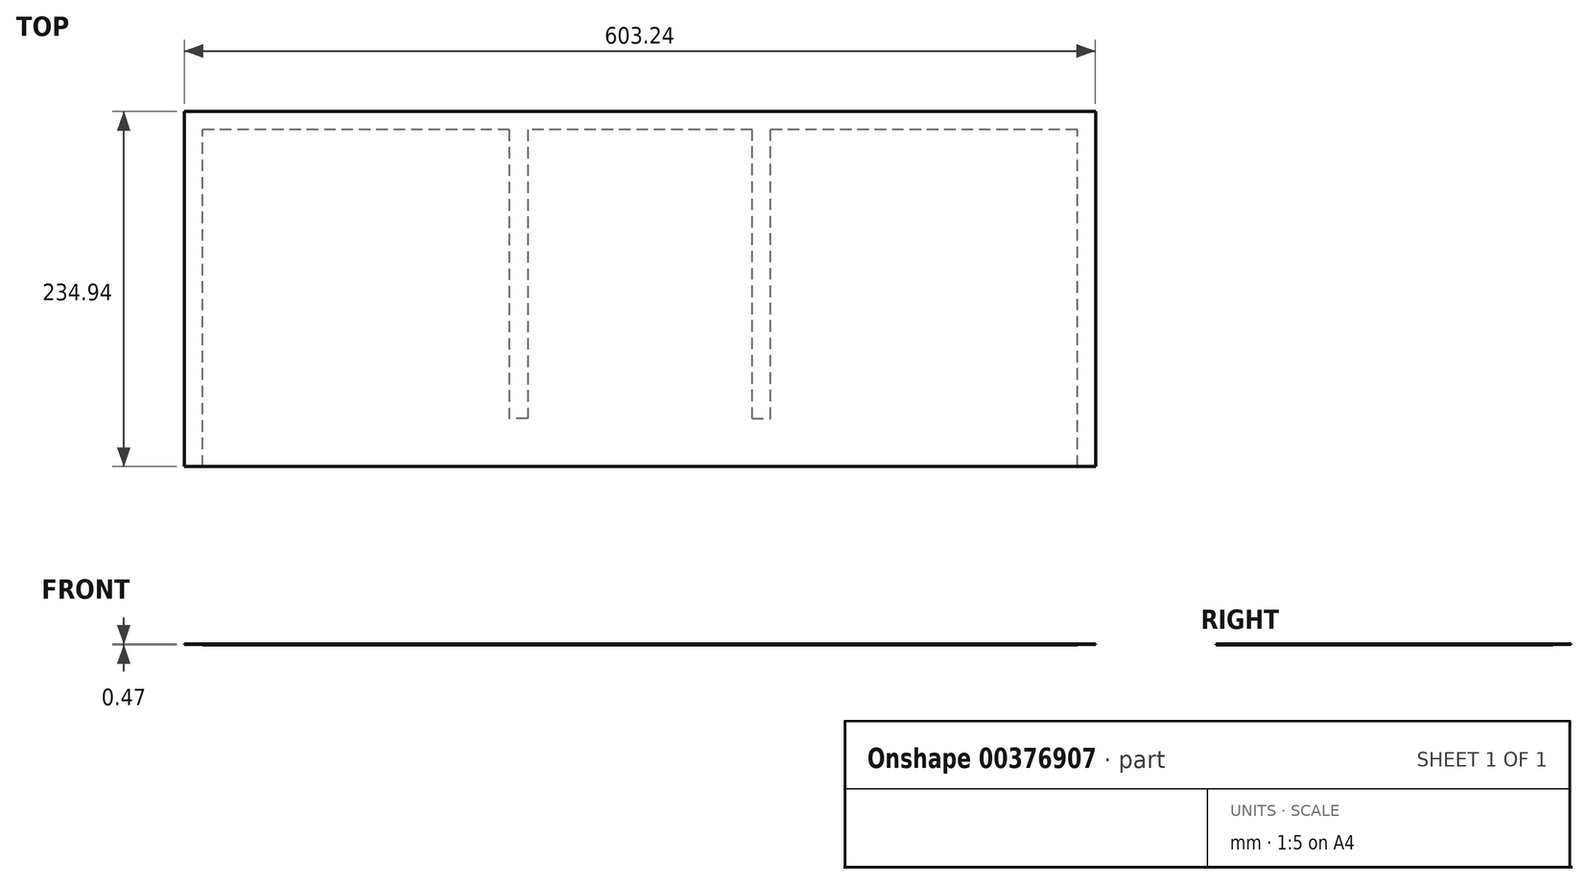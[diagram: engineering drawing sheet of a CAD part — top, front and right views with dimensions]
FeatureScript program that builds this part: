
annotation { "Feature Type Name" : "Feature", "Feature Type Description" : "" }
export const myFeature = defineFeature(function(context is Context, id is Id, definition is map)
    precondition{}
    {
        {
            assignVariable(context, id + "F0", {"name" : "material", "anyValue" : 0.47});
        }
        {
            var Q0;
            Q0=qCreatedBy(makeId("Top.planeOp"),FACE);
            var sketch = newSketch(context, id + "F1", { "sketchPlane" : qUnion([Q0])});
            skLineSegment(sketch, "E0.bottom", {"start": v(301.63, 117.48) * mm, "end": v(-301.63, 117.48) * mm});
            skLineSegment(sketch, "E0.top", {"start": v(301.63, -117.48) * mm, "end": v(-301.63, -117.48) * mm});
            skLineSegment(sketch, "E0.left", {"start": v(301.63, 117.48) * mm, "end": v(301.63, -117.48) * mm});
            skLineSegment(sketch, "E0.right", {"start": v(-301.63, 117.48) * mm, "end": v(-301.63, -117.48) * mm});
            skPoint(sketch, "E0.middle", {"position": v(0, 0) * mm});
            skSolve(sketch);
        }
        {
            var Q0;
            Q0=makeQuery(id+"F1.imprint","IMPRINT",FACE,{"disambiguationData":[TD([[makeQuery(id+"F1.imprint","IMPRINT",EDGE,{"derivedFrom":sQuery(id+"F1.wireOp",EDGE,"E0.bottom")}),1.0]])]});
            extrude(context, id + "F2", {"entities" : qUnion([Q0]), "depth" : (getVariable(context, 'material')) * mm});
        }
        {
            var Q0;
            Q0=makeQuery(id+"F2.opExtrude","CAP_FACE",FACE,{"disambiguationData":[OSD([sQuery(id+"F1.wireOp",EDGE,"E0.bottom"),sQuery(id+"F1.wireOp",EDGE,"E0.top"),sQuery(id+"F1.wireOp",EDGE,"E0.left"),sQuery(id+"F1.wireOp",EDGE,"E0.right")])],"isStart":true});
            var sketch = newSketch(context, id + "F3", { "sketchPlane" : qUnion([Q0])});
            skLineSegment(sketch, "E1.bottom", {"start": v(-301.63, 117.48) * mm, "end": v(-289.56, 117.48) * mm});
            skLineSegment(sketch, "E1.top", {"start": v(-301.63, -117.48) * mm, "end": v(-289.56, -117.48) * mm});
            skLineSegment(sketch, "E1.left", {"start": v(-301.63, 117.48) * mm, "end": v(-301.63, -117.48) * mm});
            skLineSegment(sketch, "E1.right", {"start": v(-289.56, 117.48) * mm, "end": v(-289.56, -117.48) * mm});
            skSolve(sketch);
        }
        {
            var Q0;
            Q0=makeQuery(id+"F3.imprint","IMPRINT",FACE,{"disambiguationData":[TD([[makeQuery(id+"F3.imprint","IMPRINT",EDGE,{"derivedFrom":sQuery(id+"F3.wireOp",EDGE,"E1.bottom")}),1.0]])]});
            extrude(context, id + "F4", {"entities" : qUnion([Q0]), "operationType" : NewBodyOperationType.REMOVE, "oppositeDirection" : true, "depth" : (getVariable(context, 'material') / 2) * mm});
        }
        {
            var Q0;
            Q0=makeQuery(id+"F2.opExtrude","CAP_FACE",FACE,{"disambiguationData":[OSD([sQuery(id+"F1.wireOp",EDGE,"E0.bottom"),sQuery(id+"F1.wireOp",EDGE,"E0.top"),sQuery(id+"F1.wireOp",EDGE,"E0.left"),sQuery(id+"F1.wireOp",EDGE,"E0.right")])],"isStart":true});
            var sketch = newSketch(context, id + "F5", { "sketchPlane" : qUnion([Q0])});
            skLineSegment(sketch, "E2.bottom", {"start": v(301.63, 117.48) * mm, "end": v(289.56, 117.48) * mm});
            skLineSegment(sketch, "E2.top", {"start": v(301.63, -117.48) * mm, "end": v(289.56, -117.48) * mm});
            skLineSegment(sketch, "E2.left", {"start": v(301.63, 117.48) * mm, "end": v(301.63, -117.48) * mm});
            skLineSegment(sketch, "E2.right", {"start": v(289.56, 117.48) * mm, "end": v(289.56, -117.48) * mm});
            skSolve(sketch);
        }
        {
            var Q0;
            Q0 = qSketchRegion(id + "F5", true);
            extrude(context, id + "F6", {"entities" : qUnion([Q0]), "operationType" : NewBodyOperationType.REMOVE, "oppositeDirection" : true, "depth" : (getVariable(context, 'material') / 2) * mm});
        }
        {
            var Q0;
            Q0=makeQuery(id+"F2.opExtrude","CAP_FACE",FACE,{"disambiguationData":[OSD([sQuery(id+"F1.wireOp",EDGE,"E0.bottom"),sQuery(id+"F1.wireOp",EDGE,"E0.top"),sQuery(id+"F1.wireOp",EDGE,"E0.left"),sQuery(id+"F1.wireOp",EDGE,"E0.right")])],"isStart":true});
            var sketch = newSketch(context, id + "F7", { "sketchPlane" : qUnion([Q0])});
            skLineSegment(sketch, "E3", {"start": v(289.56, 117.48) * mm, "end": v(86.36, 117.48) * mm, "construction": true});
            skLineSegment(sketch, "E4.bottom", {"start": v(86.36, 117.48) * mm, "end": v(74.3, 117.48) * mm});
            skLineSegment(sketch, "E4.top", {"start": v(86.36, -117.48) * mm, "end": v(74.3, -117.48) * mm});
            skLineSegment(sketch, "E4.left", {"start": v(86.36, 117.48) * mm, "end": v(86.36, -117.48) * mm});
            skLineSegment(sketch, "E4.right", {"start": v(74.3, 117.48) * mm, "end": v(74.3, -117.48) * mm});
            skSolve(sketch);
        }
        {
            var Q0;
            Q0 = qSketchRegion(id + "F7", true);
            extrude(context, id + "F8", {"entities" : qUnion([Q0]), "operationType" : NewBodyOperationType.REMOVE, "oppositeDirection" : true, "depth" : (getVariable(context, 'material') / 2) * mm});
        }
        {
            var Q0;
            {var subQ0=sQuery(id+"F1.wireOp",EDGE,"E0.bottom");var subQ1=sQuery(id+"F1.wireOp",EDGE,"E0.top");Q0=makeQuery(id+"F8.boolean.opBoolean","SPLIT",FACE,{"disambiguationData":[TD([makeQuery(id+"F4.boolean.opBoolean","COPY",FACE,{"derivedFrom":makeQuery(id+"F4.opExtrude","SWEPT_FACE",FACE,{"disambiguationData":[OSD([sQuery(id+"F3.wireOp",EDGE,"E1.right")])]})})])],"derivedFrom":makeQuery(id+"F2.opExtrude","CAP_FACE",FACE,{"disambiguationData":[OSD([subQ0,subQ1,sQuery(id+"F1.wireOp",EDGE,"E0.left"),sQuery(id+"F1.wireOp",EDGE,"E0.right")])],"isStart":true})});}
            var sketch = newSketch(context, id + "F9", { "sketchPlane" : qUnion([Q0])});
            skLineSegment(sketch, "E5", {"start": v(-289.56, -117.48) * mm, "end": v(-86.36, -117.48) * mm, "construction": true});
            skLineSegment(sketch, "E6.bottom", {"start": v(-86.36, -117.48) * mm, "end": v(-74.3, -117.48) * mm});
            skLineSegment(sketch, "E6.top", {"start": v(-86.36, 117.48) * mm, "end": v(-74.3, 117.48) * mm});
            skLineSegment(sketch, "E6.left", {"start": v(-86.36, -117.48) * mm, "end": v(-86.36, 117.48) * mm});
            skLineSegment(sketch, "E6.right", {"start": v(-74.3, -117.48) * mm, "end": v(-74.3, 117.48) * mm});
            skSolve(sketch);
        }
        {
            var Q0;
            Q0=makeQuery(id+"F9.imprint","IMPRINT",FACE,{"disambiguationData":[TD([[makeQuery(id+"F9.imprint","IMPRINT",EDGE,{"derivedFrom":sQuery(id+"F9.wireOp",EDGE,"E6.bottom")}),-1.0]])]});
            extrude(context, id + "F10", {"entities" : qUnion([Q0]), "operationType" : NewBodyOperationType.REMOVE, "oppositeDirection" : true, "depth" : (getVariable(context, 'material') / 2) * mm});
        }
        {
            var Q0;
            {var subQ0=sQuery(id+"F1.wireOp",EDGE,"E0.bottom");var subQ1=sQuery(id+"F1.wireOp",EDGE,"E0.top");Q0=makeQuery(id+"F8.boolean.opBoolean","SPLIT",FACE,{"disambiguationData":[TD([makeQuery(id+"F6.boolean.opBoolean","COPY",FACE,{"derivedFrom":makeQuery(id+"F6.opExtrude","SWEPT_FACE",FACE,{"disambiguationData":[OSD([sQuery(id+"F5.wireOp",EDGE,"E2.right")])]})})])],"derivedFrom":makeQuery(id+"F2.opExtrude","CAP_FACE",FACE,{"disambiguationData":[OSD([subQ0,subQ1,sQuery(id+"F1.wireOp",EDGE,"E0.left"),sQuery(id+"F1.wireOp",EDGE,"E0.right")])],"isStart":true})});}
            var sketch = newSketch(context, id + "F11", { "sketchPlane" : qUnion([Q0])});
            skLineSegment(sketch, "E7.bottom", {"start": v(289.56, -117.48) * mm, "end": v(86.36, -117.48) * mm});
            skLineSegment(sketch, "E7.top", {"start": v(289.56, -105.41) * mm, "end": v(86.36, -105.41) * mm});
            skLineSegment(sketch, "E7.left", {"start": v(289.56, -117.48) * mm, "end": v(289.56, -105.41) * mm});
            skLineSegment(sketch, "E7.right", {"start": v(86.36, -117.48) * mm, "end": v(86.36, -105.41) * mm});
            skSolve(sketch);
        }
        {
            var Q0;
            {var subQ0=sQuery(id+"F1.wireOp",EDGE,"E0.bottom");var subQ2=sQuery(id+"F1.wireOp",EDGE,"E0.top");var subQ4=makeQuery(id+"F8.opExtrude","SWEPT_FACE",FACE,{"disambiguationData":[OSD([sQuery(id+"F7.wireOp",EDGE,"E4.right")])]});Q0=makeQuery(id+"F10.boolean.opBoolean","SPLIT",FACE,{"disambiguationData":[TD([makeQuery(id+"F8.boolean.opBoolean","COPY",FACE,{"derivedFrom":subQ4})])],"derivedFrom":makeQuery(id+"F8.boolean.opBoolean","SPLIT",FACE,{"disambiguationData":[TD([makeQuery(id+"F4.boolean.opBoolean","COPY",FACE,{"derivedFrom":makeQuery(id+"F4.opExtrude","SWEPT_FACE",FACE,{"disambiguationData":[OSD([sQuery(id+"F3.wireOp",EDGE,"E1.right")])]})})])],"derivedFrom":makeQuery(id+"F2.opExtrude","CAP_FACE",FACE,{"disambiguationData":[OSD([subQ0,subQ2,sQuery(id+"F1.wireOp",EDGE,"E0.left"),sQuery(id+"F1.wireOp",EDGE,"E0.right")])],"isStart":true})})});}
            var sketch = newSketch(context, id + "F12", { "sketchPlane" : qUnion([Q0])});
            skLineSegment(sketch, "E8.bottom", {"start": v(74.3, -117.48) * mm, "end": v(-74.3, -117.48) * mm});
            skLineSegment(sketch, "E8.top", {"start": v(74.3, -105.41) * mm, "end": v(-74.3, -105.41) * mm});
            skLineSegment(sketch, "E8.left", {"start": v(74.3, -117.48) * mm, "end": v(74.3, -105.41) * mm});
            skLineSegment(sketch, "E8.right", {"start": v(-74.3, -117.48) * mm, "end": v(-74.3, -105.41) * mm});
            skSolve(sketch);
        }
        {
            var Q0;
            {var subQ0=sQuery(id+"F1.wireOp",EDGE,"E0.bottom");var subQ2=makeQuery(id+"F4.boolean.opBoolean","COPY",FACE,{"derivedFrom":makeQuery(id+"F4.opExtrude","SWEPT_FACE",FACE,{"disambiguationData":[OSD([sQuery(id+"F3.wireOp",EDGE,"E1.right")])]})});var subQ3=sQuery(id+"F1.wireOp",EDGE,"E0.top");Q0=makeQuery(id+"F10.boolean.opBoolean","SPLIT",FACE,{"disambiguationData":[TD([subQ2])],"derivedFrom":makeQuery(id+"F8.boolean.opBoolean","SPLIT",FACE,{"disambiguationData":[TD([subQ2])],"derivedFrom":makeQuery(id+"F2.opExtrude","CAP_FACE",FACE,{"disambiguationData":[OSD([subQ0,subQ3,sQuery(id+"F1.wireOp",EDGE,"E0.left"),sQuery(id+"F1.wireOp",EDGE,"E0.right")])],"isStart":true})})});}
            var sketch = newSketch(context, id + "F13", { "sketchPlane" : qUnion([Q0])});
            skLineSegment(sketch, "E9.bottom", {"start": v(-86.36, -117.48) * mm, "end": v(-289.56, -117.48) * mm});
            skLineSegment(sketch, "E9.top", {"start": v(-86.36, -105.41) * mm, "end": v(-289.56, -105.41) * mm});
            skLineSegment(sketch, "E9.left", {"start": v(-86.36, -117.48) * mm, "end": v(-86.36, -105.41) * mm});
            skLineSegment(sketch, "E9.right", {"start": v(-289.56, -117.48) * mm, "end": v(-289.56, -105.41) * mm});
            skSolve(sketch);
        }
        {
            var Q0;
            Q0=makeQuery(id+"F11.imprint","IMPRINT",FACE,{"disambiguationData":[TD([[makeQuery(id+"F11.imprint","IMPRINT",EDGE,{"derivedFrom":sQuery(id+"F11.wireOp",EDGE,"E7.bottom")}),-1.0]])]});
            extrude(context, id + "F14", {"entities" : qUnion([Q0]), "operationType" : NewBodyOperationType.REMOVE, "oppositeDirection" : true, "depth" : (getVariable(context, 'material') / 2) * mm});
        }
        {
            var Q0;
            Q0=makeQuery(id+"F12.imprint","IMPRINT",FACE,{"disambiguationData":[TD([[makeQuery(id+"F12.imprint","IMPRINT",EDGE,{"derivedFrom":sQuery(id+"F12.wireOp",EDGE,"E8.bottom")}),-1.0]])]});
            extrude(context, id + "F15", {"entities" : qUnion([Q0]), "operationType" : NewBodyOperationType.REMOVE, "oppositeDirection" : true, "depth" : (getVariable(context, 'material') / 2) * mm});
        }
        {
            var Q0;
            Q0=makeQuery(id+"F13.imprint","IMPRINT",FACE,{"disambiguationData":[TD([[makeQuery(id+"F13.imprint","IMPRINT",EDGE,{"derivedFrom":sQuery(id+"F13.wireOp",EDGE,"E9.bottom")}),-1.0]])]});
            extrude(context, id + "F16", {"entities" : qUnion([Q0]), "operationType" : NewBodyOperationType.REMOVE, "oppositeDirection" : true, "depth" : (getVariable(context, 'material') / 2) * mm});
        }
        {
            var Q0;
            Q0=makeQuery(id+"F16.boolean.opBoolean","MERGE",FACE,{"derivedFrom":[makeQuery(id+"F4.boolean.opBoolean","COPY",FACE,{"derivedFrom":makeQuery(id+"F4.opExtrude","CAP_FACE",FACE,{"disambiguationData":[OSD([sQuery(id+"F3.wireOp",EDGE,"E1.bottom"),sQuery(id+"F3.wireOp",EDGE,"E1.top"),sQuery(id+"F3.wireOp",EDGE,"E1.left"),sQuery(id+"F3.wireOp",EDGE,"E1.right")])],"isStart":false})}),makeQuery(id+"F15.boolean.opBoolean","MERGE",FACE,{"derivedFrom":[makeQuery(id+"F10.boolean.opBoolean","COPY",FACE,{"derivedFrom":makeQuery(id+"F10.opExtrude","CAP_FACE",FACE,{"disambiguationData":[OSD([sQuery(id+"F9.wireOp",EDGE,"E6.bottom"),sQuery(id+"F9.wireOp",EDGE,"E6.top"),sQuery(id+"F9.wireOp",EDGE,"E6.left"),sQuery(id+"F9.wireOp",EDGE,"E6.right")])],"isStart":false})}),makeQuery(id+"F14.boolean.opBoolean","MERGE",FACE,{"derivedFrom":[makeQuery(id+"F6.boolean.opBoolean","COPY",FACE,{"derivedFrom":makeQuery(id+"F6.opExtrude","CAP_FACE",FACE,{"disambiguationData":[OSD([sQuery(id+"F5.wireOp",EDGE,"E2.bottom"),sQuery(id+"F5.wireOp",EDGE,"E2.top"),sQuery(id+"F5.wireOp",EDGE,"E2.left"),sQuery(id+"F5.wireOp",EDGE,"E2.right")])],"isStart":false})}),makeQuery(id+"F8.boolean.opBoolean","COPY",FACE,{"derivedFrom":makeQuery(id+"F8.opExtrude","CAP_FACE",FACE,{"disambiguationData":[OSD([sQuery(id+"F7.wireOp",EDGE,"E4.bottom"),sQuery(id+"F7.wireOp",EDGE,"E4.top"),sQuery(id+"F7.wireOp",EDGE,"E4.left"),sQuery(id+"F7.wireOp",EDGE,"E4.right")])],"isStart":false})}),makeQuery(id+"F14.opExtrude","CAP_FACE",FACE,{"disambiguationData":[OSD([sQuery(id+"F11.wireOp",EDGE,"E7.bottom"),sQuery(id+"F11.wireOp",EDGE,"E7.top"),sQuery(id+"F11.wireOp",EDGE,"E7.left"),sQuery(id+"F11.wireOp",EDGE,"E7.right")])],"isStart":false})]}),makeQuery(id+"F15.opExtrude","CAP_FACE",FACE,{"disambiguationData":[OSD([sQuery(id+"F12.wireOp",EDGE,"E8.bottom"),sQuery(id+"F12.wireOp",EDGE,"E8.top"),sQuery(id+"F12.wireOp",EDGE,"E8.left"),sQuery(id+"F12.wireOp",EDGE,"E8.right")])],"isStart":false})]}),makeQuery(id+"F16.opExtrude","CAP_FACE",FACE,{"disambiguationData":[OSD([sQuery(id+"F13.wireOp",EDGE,"E9.bottom"),sQuery(id+"F13.wireOp",EDGE,"E9.top"),sQuery(id+"F13.wireOp",EDGE,"E9.left"),sQuery(id+"F13.wireOp",EDGE,"E9.right")])],"isStart":false})]});
            var sketch = newSketch(context, id + "F17", { "sketchPlane" : qUnion([Q0])});
            skLineSegment(sketch, "E10.bottom", {"start": v(74.3, 117.48) * mm, "end": v(86.36, 117.48) * mm});
            skLineSegment(sketch, "E10.top", {"start": v(74.3, 85.73) * mm, "end": v(86.36, 85.73) * mm});
            skLineSegment(sketch, "E10.left", {"start": v(74.3, 117.48) * mm, "end": v(74.3, 85.73) * mm});
            skLineSegment(sketch, "E10.right", {"start": v(86.36, 117.48) * mm, "end": v(86.36, 85.73) * mm});
            skSolve(sketch);
        }
        {
            var Q0;
            Q0 = qSketchRegion(id + "F17", true);
            extrude(context, id + "F18", {"entities" : qUnion([Q0]), "operationType" : NewBodyOperationType.ADD, "depth" : (getVariable(context, 'material') / 2) * mm});
        }
        {
            var Q0;
            Q0=makeQuery(id+"F16.boolean.opBoolean","MERGE",FACE,{"derivedFrom":[makeQuery(id+"F4.boolean.opBoolean","COPY",FACE,{"derivedFrom":makeQuery(id+"F4.opExtrude","CAP_FACE",FACE,{"disambiguationData":[OSD([sQuery(id+"F3.wireOp",EDGE,"E1.bottom"),sQuery(id+"F3.wireOp",EDGE,"E1.top"),sQuery(id+"F3.wireOp",EDGE,"E1.left"),sQuery(id+"F3.wireOp",EDGE,"E1.right")])],"isStart":false})}),makeQuery(id+"F15.boolean.opBoolean","MERGE",FACE,{"derivedFrom":[makeQuery(id+"F10.boolean.opBoolean","COPY",FACE,{"derivedFrom":makeQuery(id+"F10.opExtrude","CAP_FACE",FACE,{"disambiguationData":[OSD([sQuery(id+"F9.wireOp",EDGE,"E6.bottom"),sQuery(id+"F9.wireOp",EDGE,"E6.top"),sQuery(id+"F9.wireOp",EDGE,"E6.left"),sQuery(id+"F9.wireOp",EDGE,"E6.right")])],"isStart":false})}),makeQuery(id+"F14.boolean.opBoolean","MERGE",FACE,{"derivedFrom":[makeQuery(id+"F6.boolean.opBoolean","COPY",FACE,{"derivedFrom":makeQuery(id+"F6.opExtrude","CAP_FACE",FACE,{"disambiguationData":[OSD([sQuery(id+"F5.wireOp",EDGE,"E2.bottom"),sQuery(id+"F5.wireOp",EDGE,"E2.top"),sQuery(id+"F5.wireOp",EDGE,"E2.left"),sQuery(id+"F5.wireOp",EDGE,"E2.right")])],"isStart":false})}),makeQuery(id+"F8.boolean.opBoolean","COPY",FACE,{"derivedFrom":makeQuery(id+"F8.opExtrude","CAP_FACE",FACE,{"disambiguationData":[OSD([sQuery(id+"F7.wireOp",EDGE,"E4.bottom"),sQuery(id+"F7.wireOp",EDGE,"E4.top"),sQuery(id+"F7.wireOp",EDGE,"E4.left"),sQuery(id+"F7.wireOp",EDGE,"E4.right")])],"isStart":false})}),makeQuery(id+"F14.opExtrude","CAP_FACE",FACE,{"disambiguationData":[OSD([sQuery(id+"F11.wireOp",EDGE,"E7.bottom"),sQuery(id+"F11.wireOp",EDGE,"E7.top"),sQuery(id+"F11.wireOp",EDGE,"E7.left"),sQuery(id+"F11.wireOp",EDGE,"E7.right")])],"isStart":false})]}),makeQuery(id+"F15.opExtrude","CAP_FACE",FACE,{"disambiguationData":[OSD([sQuery(id+"F12.wireOp",EDGE,"E8.bottom"),sQuery(id+"F12.wireOp",EDGE,"E8.top"),sQuery(id+"F12.wireOp",EDGE,"E8.left"),sQuery(id+"F12.wireOp",EDGE,"E8.right")])],"isStart":false})]}),makeQuery(id+"F16.opExtrude","CAP_FACE",FACE,{"disambiguationData":[OSD([sQuery(id+"F13.wireOp",EDGE,"E9.bottom"),sQuery(id+"F13.wireOp",EDGE,"E9.top"),sQuery(id+"F13.wireOp",EDGE,"E9.left"),sQuery(id+"F13.wireOp",EDGE,"E9.right")])],"isStart":false})]});
            var sketch = newSketch(context, id + "F19", { "sketchPlane" : qUnion([Q0])});
            skLineSegment(sketch, "E11.bottom", {"start": v(-74.3, 117.48) * mm, "end": v(-86.36, 117.48) * mm});
            skLineSegment(sketch, "E11.top", {"start": v(-74.3, 85.73) * mm, "end": v(-86.36, 85.73) * mm});
            skLineSegment(sketch, "E11.left", {"start": v(-74.3, 117.48) * mm, "end": v(-74.3, 85.73) * mm});
            skLineSegment(sketch, "E11.right", {"start": v(-86.36, 117.48) * mm, "end": v(-86.36, 85.73) * mm});
            skSolve(sketch);
        }
        {
            var Q0;
            Q0 = qSketchRegion(id + "F19", true);
            extrude(context, id + "F20", {"entities" : qUnion([Q0]), "operationType" : NewBodyOperationType.ADD, "depth" : (getVariable(context, 'material') / 2) * mm});
        }
    });
